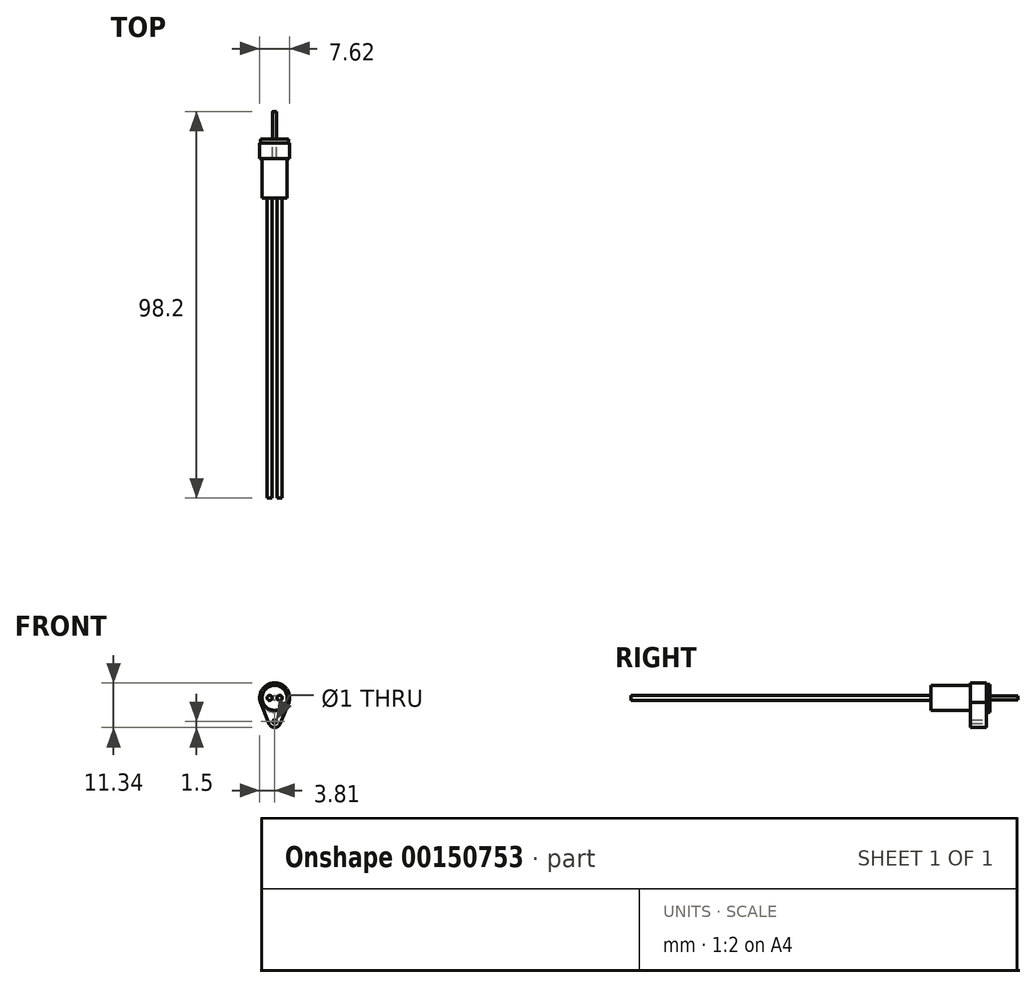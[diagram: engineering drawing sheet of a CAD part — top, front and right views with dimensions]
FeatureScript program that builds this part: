
annotation { "Feature Type Name" : "Feature", "Feature Type Description" : "" }
export const myFeature = defineFeature(function(context is Context, id is Id, definition is map)
    precondition{}
    {
        {
            var Q0;
            Q0=qCreatedBy(makeId("Front.planeOp"),FACE);
            var sketch = newSketch(context, id + "F0", { "sketchPlane" : qUnion([Q0])});
            skCircle(sketch, "E0", {"center": v(0, 0) * mm, "radius": 3.18 * mm});
            skSolve(sketch);
        }
        {
            var Q0;
            Q0=makeQuery(id+"F0.imprint","IMPRINT",FACE,{"disambiguationData":[TD([[makeQuery(id+"F0.imprint","IMPRINT",EDGE,{"derivedFrom":sQuery(id+"F0.wireOp",EDGE,"E0")}),1.0]])]});
            extrude(context, id + "F1", {"entities" : qUnion([Q0]), "depth" : 15 * mm});
        }
        {
            var Q0;
            Q0=makeQuery(id+"F1.opExtrude","CAP_FACE",FACE,{"disambiguationData":[OSD([sQuery(id+"F0.wireOp",EDGE,"E0")])],"isStart":true});
            var sketch = newSketch(context, id + "F2", { "sketchPlane" : qUnion([Q0])});
            skCircle(sketch, "E1", {"center": v(0, 0) * mm, "radius": 0.5 * mm});
            skSolve(sketch);
        }
        {
            var Q0;
            Q0=makeQuery(id+"F2.imprint","IMPRINT",FACE,{"disambiguationData":[TD([[makeQuery(id+"F2.imprint","IMPRINT",EDGE,{"derivedFrom":sQuery(id+"F2.wireOp",EDGE,"E1")}),1.0]])]});
            extrude(context, id + "F3", {"entities" : qUnion([Q0]), "operationType" : NewBodyOperationType.ADD, "depth" : 7 * mm});
        }
        {
            var Q0;
            Q0=makeQuery(id+"F1.opExtrude","CAP_FACE",FACE,{"disambiguationData":[OSD([sQuery(id+"F0.wireOp",EDGE,"E0")])],"isStart":true});
            var sketch = newSketch(context, id + "F4", { "sketchPlane" : qUnion([Q0])});
            skArc(sketch, "E2", {"start": v(3.4, -1.7) * mm, "mid": v(0, 3.8) * mm, "end": v(-3.4, -1.7) * mm});
            skCircle(sketch, "E3", {"center": v(0, 0) * mm, "radius": 3.18 * mm});
            skCircle(sketch, "E4", {"center": v(0, -6.03) * mm, "radius": 0.5 * mm});
            skArc(sketch, "E5", {"start": v(-1.39, -6.6) * mm, "mid": v(0, -7.53) * mm, "end": v(1.39, -6.6) * mm});
            skLineSegment(sketch, "E6", {"start": v(-1.39, -6.6) * mm, "end": v(-3.62, -1.19) * mm});
            skLineSegment(sketch, "E7", {"start": v(-1.39, -6.6) * mm, "end": v(1.39, -6.6) * mm, "construction": true});
            skLineSegment(sketch, "E8", {"start": v(-3.62, -1.19) * mm, "end": v(3.62, -1.19) * mm, "construction": true});
            skLineSegment(sketch, "E9", {"start": v(3.62, -1.19) * mm, "end": v(1.39, -6.6) * mm});
            skSolve(sketch);
        }
        {
            var Q0;
            Q0=makeQuery(id+"F4.imprint","IMPRINT",FACE,{"disambiguationData":[TD([[makeQuery(id+"F4.imprint","IMPRINT",EDGE,{"derivedFrom":sQuery(id+"F4.wireOp",EDGE,"E3")}),1.0]])]});
            extrude(context, id + "F5", {"entities" : qUnion([Q0]), "operationType" : NewBodyOperationType.ADD, "oppositeDirection" : true, "depth" : 5 * mm});
        }
        {
            var Q0;
            Q0=makeQuery(id+"F5.boolean.opBoolean","MERGE",FACE,{"derivedFrom":[makeQuery(id+"F1.opExtrude","CAP_FACE",FACE,{"disambiguationData":[OSD([sQuery(id+"F0.wireOp",EDGE,"E0")])],"isStart":true}),makeQuery(id+"F5.opExtrude","CAP_FACE",FACE,{"disambiguationData":[OSD([sQuery(id+"F4.wireOp",EDGE,"E2"),sQuery(id+"F4.wireOp",EDGE,"E3"),sQuery(id+"F4.wireOp",EDGE,"E4"),sQuery(id+"F4.wireOp",EDGE,"E5"),sQuery(id+"F4.wireOp",EDGE,"E6"),sQuery(id+"F4.wireOp",EDGE,"E9")])],"isStart":true})]});
            var sketch = newSketch(context, id + "F6", { "sketchPlane" : qUnion([Q0])});
            skCircle(sketch, "E10", {"center": v(0, -0.12) * mm, "radius": 3.53 * mm});
            skCircle(sketch, "E11", {"center": v(0, 0) * mm, "radius": 9.32 * mm});
            skSolve(sketch);
        }
        {
            var Q0;
            Q0 = qSketchRegion(id + "F6", true);
            extrude(context, id + "F7", {"entities" : qUnion([Q0]), "operationType" : NewBodyOperationType.REMOVE, "oppositeDirection" : true, "depth" : 1 * mm});
        }
        {
            var Q0;
            Q0=makeQuery(id+"F1.opExtrude","CAP_FACE",FACE,{"disambiguationData":[OSD([sQuery(id+"F0.wireOp",EDGE,"E0")])],"isStart":false});
            var sketch = newSketch(context, id + "F8", { "sketchPlane" : qUnion([Q0])});
            skCircle(sketch, "E12", {"center": v(-1.27, 0) * mm, "radius": 0.64 * mm});
            skCircle(sketch, "E13", {"center": v(1.27, 0) * mm, "radius": 0.66 * mm});
            skSolve(sketch);
        }
        {
            var Q0;
            Q0=makeQuery(id+"F8.imprint","IMPRINT",FACE,{"disambiguationData":[TD([[makeQuery(id+"F8.imprint","IMPRINT",EDGE,{"derivedFrom":sQuery(id+"F8.wireOp",EDGE,"E12")}),1.0]])]});
            var Q1;
            Q1=makeQuery(id+"F8.imprint","IMPRINT",FACE,{"disambiguationData":[TD([[makeQuery(id+"F8.imprint","IMPRINT",EDGE,{"derivedFrom":sQuery(id+"F8.wireOp",EDGE,"E13")}),1.0]])]});
            extrude(context, id + "F9", {"entities" : qUnion([Q0, Q1]), "operationType" : NewBodyOperationType.ADD, "depth" : 76.2 * mm});
        }
    });
